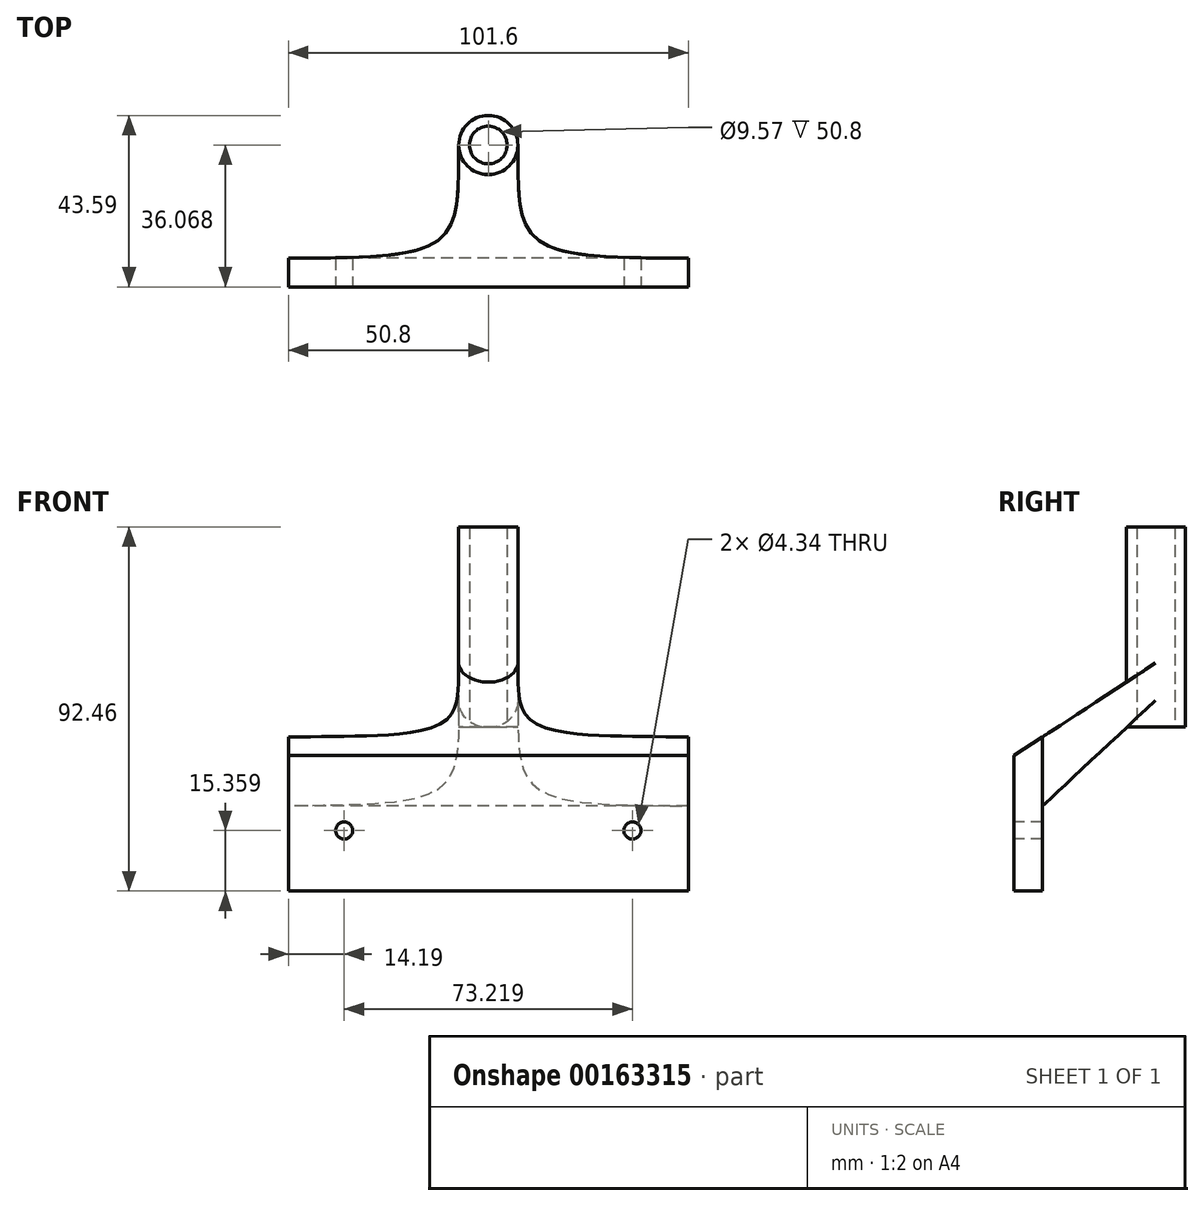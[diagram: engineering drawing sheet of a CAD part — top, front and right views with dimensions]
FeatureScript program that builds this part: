
annotation { "Feature Type Name" : "Feature", "Feature Type Description" : "" }
export const myFeature = defineFeature(function(context is Context, id is Id, definition is map)
    precondition{}
    {
        {
            var Q0;
            Q0=qCreatedBy(makeId("Right.planeOp"),FACE);
            var sketch = newSketch(context, id + "F0", { "sketchPlane" : qUnion([Q0])});
            skLineSegment(sketch, "E0", {"start": v(0, 0) * mm, "end": v(0, 0) * mm});
            skLineSegment(sketch, "E1", {"start": v(0, 0) * mm, "end": v(-7.3, 0) * mm});
            skLineSegment(sketch, "E2", {"start": v(-7.3, 0) * mm, "end": v(-7.3, 34.4) * mm});
            skLineSegment(sketch, "E3", {"start": v(-7.3, 34.4) * mm, "end": v(28.78, 57.94) * mm});
            skLineSegment(sketch, "E4", {"start": v(28.78, 57.94) * mm, "end": v(28.78, 48.48) * mm});
            skLineSegment(sketch, "E5", {"start": v(28.78, 48.48) * mm, "end": v(0, 21.62) * mm});
            skLineSegment(sketch, "E6", {"start": v(0, 21.62) * mm, "end": v(0, 0) * mm});
            skSolve(sketch);
        }
        {
            var Q0;
            Q0 = qSketchRegion(id + "F0", true);
            extrude(context, id + "F1", {"entities" : qUnion([Q0]), "depth" : 101.6 * mm, "symmetric" : true});
        }
        {
            var Q0;
            Q0=makeQuery(id+"F1.opExtrude","SWEPT_FACE",FACE,{"disambiguationData":[OSD([sQuery(id+"F0.wireOp",EDGE,"E1")])]});
            var sketch = newSketch(context, id + "F2", { "sketchPlane" : qUnion([Q0])});
            skLineSegment(sketch, "E7", {"start": v(0, 0) * mm, "end": v(0, -49.18) * mm, "construction": true});
            skFitSpline(sketch, "E8", {"points": [v(-7.55, -35.88) * mm, v(-59.99, 0) * mm], "startDerivative": vector(0, 107.63) * mm, "endDerivative": vector(-167.3, 0) * mm});
            skLineSegment(sketch, "E9", {"start": v(-7.55, -35.88) * mm, "end": v(-7.55, 27.82) * mm, "construction": true});
            skFitSpline(sketch, "E10.MirrorCS", {"points": [v(7.55, -35.88) * mm, v(59.99, 0) * mm], "startDerivative": vector(0, 107.63) * mm, "endDerivative": vector(167.3, 0) * mm});
            skArc(sketch, "E11", {"start": v(-59.99, 0) * mm, "mid": v(-48.97, -40.16) * mm, "end": v(-7.55, -35.88) * mm});
            skArc(sketch, "E12.MirrorCS", {"start": v(59.99, 0) * mm, "mid": v(48.97, -40.16) * mm, "end": v(7.55, -35.88) * mm});
            skSolve(sketch);
        }
        {
            var Q0;
            Q0 = qSketchRegion(id + "F2", true);
            extrude(context, id + "F3", {"entities" : qUnion([Q0]), "operationType" : NewBodyOperationType.REMOVE, "endBound" : BoundingType.THROUGH_ALL, "oppositeDirection" : true, "depth" : 25.4 * mm});
        }
        {
            var Q0;
            Q0=makeQuery(id+"F1.opExtrude","SWEPT_FACE",FACE,{"disambiguationData":[OSD([sQuery(id+"F0.wireOp",EDGE,"E1")])]});
            var sketch = newSketch(context, id + "F4", { "sketchPlane" : qUnion([Q0])});
            skLineSegment(sketch, "E13", {"start": v(0, 0) * mm, "end": v(0, -63.76) * mm, "construction": true});
            skLineSegment(sketch, "E14.0", {"start": v(7.52, -28.78) * mm, "end": v(-7.52, -28.78) * mm, "construction": true});
            skCircle(sketch, "E15", {"center": v(0, -28.78) * mm, "radius": 7.52 * mm});
            skCircle(sketch, "E16", {"center": v(0, -28.78) * mm, "radius": 4.79 * mm});
            skSolve(sketch);
        }
        {
            var Q0;
            Q0=makeQuery(id+"F4.imprint","IMPRINT",FACE,{"disambiguationData":[TD([[makeQuery(id+"F4.imprint","IMPRINT",EDGE,{"derivedFrom":sQuery(id+"F4.wireOp",EDGE,"E15")}),1.0]])]});
            extrude(context, id + "F5", {"entities" : qUnion([Q0]), "operationType" : NewBodyOperationType.ADD, "oppositeDirection" : true, "depth" : 92.46 * mm, "hasSecondDirection" : true, "secondDirectionOppositeDirection" : true, "secondDirectionDepth" : 41.66 * mm});
        }
        {
            var Q0;
            Q0=makeQuery(id+"F4.imprint","IMPRINT",FACE,{"disambiguationData":[TD([[makeQuery(id+"F4.imprint","IMPRINT",EDGE,{"derivedFrom":sQuery(id+"F4.wireOp",EDGE,"E16")}),1.0]])]});
            extrude(context, id + "F6", {"entities" : qUnion([Q0]), "operationType" : NewBodyOperationType.REMOVE, "endBound" : BoundingType.THROUGH_ALL, "oppositeDirection" : true, "depth" : 25.4 * mm});
        }
        {
            var Q0;
            Q0=makeQuery(id+"F1.opExtrude","SWEPT_FACE",FACE,{"disambiguationData":[OSD([sQuery(id+"F0.wireOp",EDGE,"E2")])]});
            var sketch = newSketch(context, id + "F7", { "sketchPlane" : qUnion([Q0])});
            skLineSegment(sketch, "E17", {"start": v(0, 0) * mm, "end": v(0, 45.74) * mm, "construction": true});
            skCircle(sketch, "E18", {"center": v(36.6, 15.36) * mm, "radius": 2.17 * mm});
            skCircle(sketch, "E19.MirrorC", {"center": v(-36.6, 15.36) * mm, "radius": 2.17 * mm});
            skSolve(sketch);
        }
        {
            var Q0;
            Q0 = qSketchRegion(id + "F7", true);
            extrude(context, id + "F8", {"entities" : qUnion([Q0]), "operationType" : NewBodyOperationType.REMOVE, "oppositeDirection" : true, "depth" : 25.4 * mm});
        }
    });
